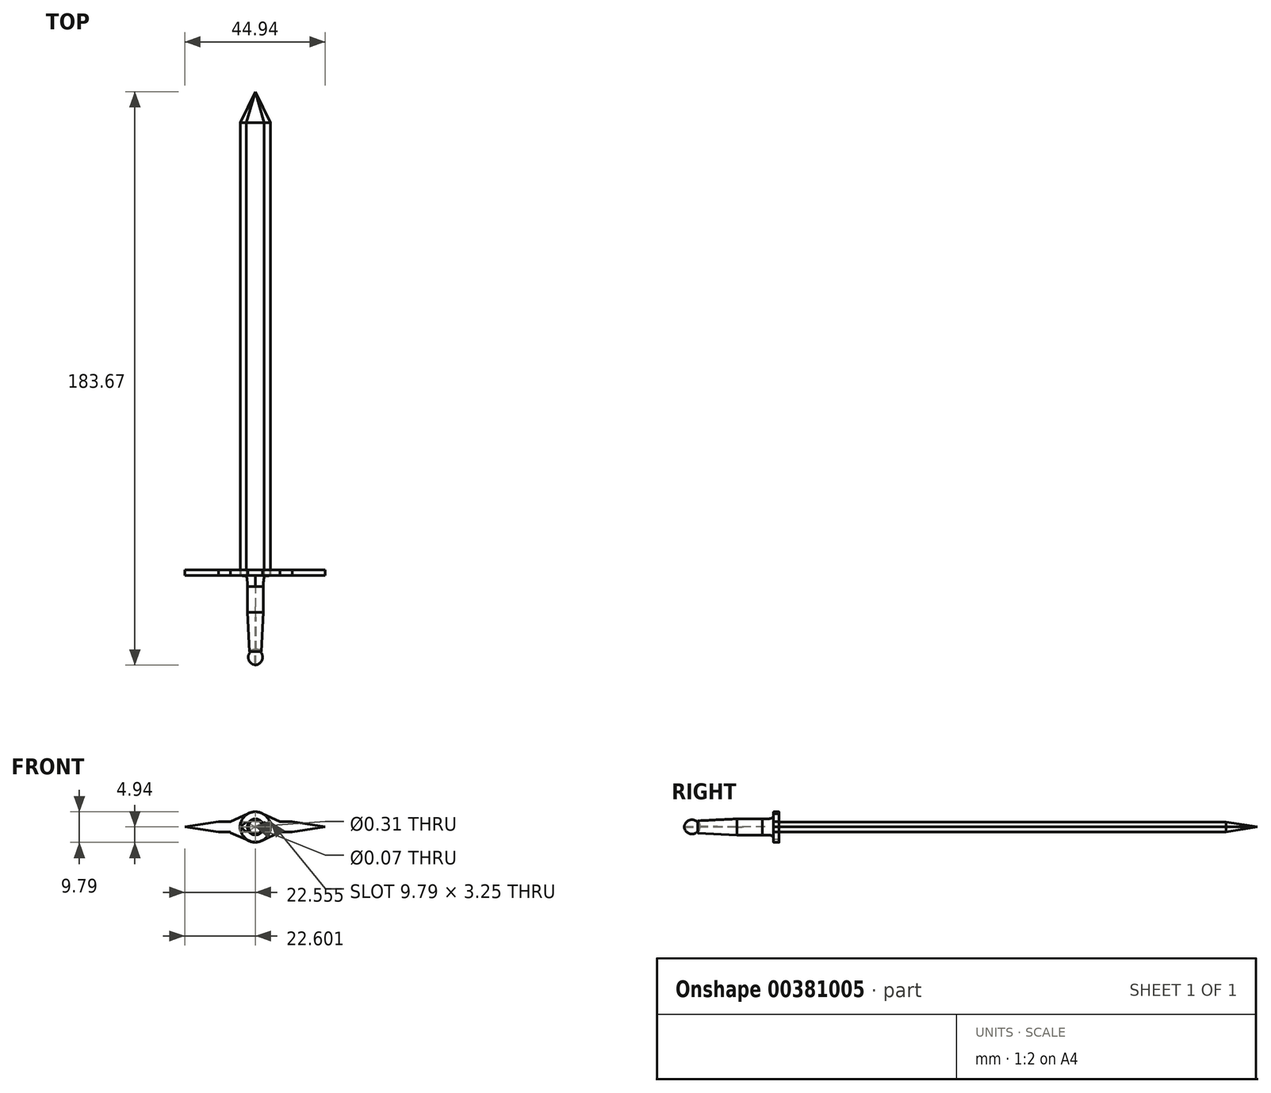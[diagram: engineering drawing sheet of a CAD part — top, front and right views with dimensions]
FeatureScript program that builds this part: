
annotation { "Feature Type Name" : "Feature", "Feature Type Description" : "" }
export const myFeature = defineFeature(function(context is Context, id is Id, definition is map)
    precondition{}
    {
        {
            var Q0;
            Q0=qCreatedBy(makeId("Top.planeOp"),FACE);
            var sketch = newSketch(context, id + "F0", { "sketchPlane" : qUnion([Q0])});
            skLineSegment(sketch, "E0", {"start": v(-127.1, -55.06) * mm, "end": v(-127.1, -61.54) * mm});
            skLineSegment(sketch, "E1", {"start": v(-127.7, -75.78) * mm, "end": v(-127.1, -63.23) * mm});
            skLineSegment(sketch, "E2", {"start": v(-124.83, -51.52) * mm, "end": v(-129.67, -51.52) * mm});
            skLineSegment(sketch, "E3", {"start": v(-129.67, -51.52) * mm, "end": v(-129.67, -54.16) * mm});
            skFitSpline(sketch, "E4", {"points": [v(-129.67, -54.16) * mm, v(-127.1, -55.06) * mm], "startDerivative": vector(4.15, -0.26) * mm, "endDerivative": vector(2.59, -2.32) * mm});
            skLineSegment(sketch, "E5", {"start": v(-127.1, -61.54) * mm, "end": v(-129.64, -61.54) * mm});
            skLineSegment(sketch, "E6", {"start": v(-129.64, -61.54) * mm, "end": v(-129.67, -54.16) * mm});
            skLineSegment(sketch, "E7", {"start": v(-129.64, -61.54) * mm, "end": v(-129.64, -63.25) * mm});
            skLineSegment(sketch, "E8", {"start": v(-129.64, -63.25) * mm, "end": v(-127.1, -63.23) * mm});
            skLineSegment(sketch, "E9", {"start": v(-129.64, -63.25) * mm, "end": v(-129.52, -75.1) * mm});
            skArc(sketch, "E10", {"start": v(-129.52, -75.1) * mm, "mid": v(-126.9, -77.63) * mm, "end": v(-129.52, -80.16) * mm});
            skLineSegment(sketch, "E11", {"start": v(-129.52, -75.1) * mm, "end": v(-129.52, -80.16) * mm});
            skLineSegment(sketch, "E12", {"start": v(-127.1, -61.54) * mm, "end": v(-127.1, -63.23) * mm});
            skFitSpline(sketch, "E13", {"points": [v(-127.1, -55.06) * mm, v(-124.83, -51.52) * mm], "startDerivative": vector(0.06, 10.63) * mm, "endDerivative": vector(6.8, 0) * mm});
            skSolve(sketch);
        }
        {
            var Q0;
            Q0=qSketchRegion(id+"F0",true);
            var Q1;
            Q1=sQuery(id+"F0.wireOp",EDGE,"E3");
            revolve(context, id + "F1", {"entities" : qUnion([Q0]), "axis" : qUnion([Q1]), "revolveType" : RevolveType.FULL});
        }
        {
            var Q0;
            {var subQ0=sQuery(id+"F0.wireOp",EDGE,"E2");Q0=makeQuery(id+"F1.opRevolve","SWEPT_FACE",FACE,{"disambiguationData":[OSD([subQ0]),TDD([makeQuery(id+"F0.imprint","IMPRINT",EDGE,{"disambiguationData":[TD([[makeQuery(id+"F0.imprint","INTERSECT",VERTEX,{"derivedFrom":[subQ0,sQuery(id+"F0.wireOp",EDGE,"E3")]}),1.0]])],"derivedFrom":subQ0})])]});}
            var sketch = newSketch(context, id + "F2", { "sketchPlane" : qUnion([Q0])});
            skLineSegment(sketch, "E14.bottom", {"start": v(141.43, 1.62) * mm, "end": v(117.91, 1.62) * mm});
            skLineSegment(sketch, "E14.top", {"start": v(141.43, -1.62) * mm, "end": v(117.91, -1.62) * mm});
            skLineSegment(sketch, "E14.left", {"start": v(141.43, 1.62) * mm, "end": v(141.43, -1.62) * mm});
            skLineSegment(sketch, "E14.right", {"start": v(117.91, 1.62) * mm, "end": v(117.91, -1.62) * mm});
            skPoint(sketch, "E14.middle", {"position": v(129.67, 0) * mm});
            skPoint(sketch, "E15.middle", {"position": v(129.67, 3.45) * mm});
            skPoint(sketch, "E16.middle", {"position": v(129.67, -1.62) * mm});
            skLineSegment(sketch, "E17", {"start": v(117.91, 1.62) * mm, "end": v(107.33, 0) * mm});
            skPoint(sketch, "E17.endSnap0", {"position": v(117.91, 0) * mm});
            skLineSegment(sketch, "E18", {"start": v(107.33, 0) * mm, "end": v(117.91, -1.62) * mm});
            skLineSegment(sketch, "E19", {"start": v(141.43, -1.62) * mm, "end": v(152.27, 0) * mm});
            skLineSegment(sketch, "E20", {"start": v(152.27, 0) * mm, "end": v(141.43, 1.62) * mm});
            skPoint(sketch, "E21", {"position": v(141.43, 0) * mm});
            skArc(sketch, "E22", {"start": v(125.1, 1.62) * mm, "mid": v(133.25, -3.43) * mm, "end": v(127.86, 4.49) * mm});
            skArc(sketch, "E23", {"start": v(127.86, 4.49) * mm, "mid": v(126.18, 3.35) * mm, "end": v(125.1, 1.62) * mm});
            skLineSegment(sketch, "E24", {"start": v(121.8, -1.62) * mm, "end": v(121.8, 1.62) * mm});
            skLineSegment(sketch, "E25", {"start": v(121.8, 1.62) * mm, "end": v(127.86, 4.49) * mm});
            skLineSegment(sketch, "E26", {"start": v(121.8, -1.62) * mm, "end": v(127.86, -4.59) * mm});
            skLineSegment(sketch, "E27", {"start": v(137.7, 1.62) * mm, "end": v(137.7, -1.91) * mm});
            skLineSegment(sketch, "E28", {"start": v(137.7, -1.91) * mm, "end": v(131.56, -4.46) * mm});
            skLineSegment(sketch, "E29", {"start": v(137.7, 1.62) * mm, "end": v(131.59, 4.47) * mm});
            skSolve(sketch);
        }
        {
            var Q0;
            Q0=qSketchRegion(id+"F2",true);
            extrude(context, id + "F3", {"entities" : qUnion([Q0]), "depth" : 1.78 * mm});
        }
        {
            var Q0;
            Q0=makeQuery(id+"F1.opRevolve","SWEPT_FACE",FACE,{"disambiguationData":[OSD([sQuery(id+"F0.wireOp",EDGE,"E2")])]});
            var sketch = newSketch(context, id + "F4", { "sketchPlane" : qUnion([Q0])});
            skLineSegment(sketch, "E30", {"start": v(124.83, 0) * mm, "end": v(126.83, 1.53) * mm});
            skLineSegment(sketch, "E31", {"start": v(124.83, 0) * mm, "end": v(126.83, -1.57) * mm});
            skLineSegment(sketch, "E32", {"start": v(134.5, 0) * mm, "end": v(132.53, 1.57) * mm});
            skLineSegment(sketch, "E33", {"start": v(134.5, 0) * mm, "end": v(132.56, -1.57) * mm});
            skLineSegment(sketch, "E34", {"start": v(132.56, -1.57) * mm, "end": v(126.83, -1.57) * mm});
            skLineSegment(sketch, "E35", {"start": v(126.83, 1.53) * mm, "end": v(132.53, 1.57) * mm});
            skSolve(sketch);
        }
        {
            var Q0;
            Q0=makeQuery(id+"F4.imprint","IMPRINT",FACE,{"disambiguationData":[TD([[makeQuery(id+"F4.imprint","IMPRINT",EDGE,{"derivedFrom":sQuery(id+"F4.wireOp",EDGE,"E30")}),-1.0]])]});
            extrude(context, id + "F5", {"entities" : qUnion([Q0]), "depth" : 145.03 * mm});
        }
        {
            var Q0;
            Q0=makeQuery(id+"F5.opExtrude","CAP_FACE",FACE,{"disambiguationData":[OSD([sQuery(id+"F4.wireOp",EDGE,"E30"),sQuery(id+"F4.wireOp",EDGE,"E31"),sQuery(id+"F4.wireOp",EDGE,"E32"),sQuery(id+"F4.wireOp",EDGE,"E33"),sQuery(id+"F4.wireOp",EDGE,"E34"),sQuery(id+"F4.wireOp",EDGE,"E35")])],"isStart":false});
            var sketch = newSketch(context, id + "F6", { "sketchPlane" : qUnion([Q0])});
            skLineSegment(sketch, "E36", {"start": v(124.83, 0) * mm, "end": v(129.4, 0) * mm});
            skLineSegment(sketch, "E37", {"start": v(129.4, 0) * mm, "end": v(134.5, 0) * mm});
            skLineSegment(sketch, "E38", {"start": v(129.4, 0) * mm, "end": v(126.83, 1.53) * mm});
            skLineSegment(sketch, "E39", {"start": v(129.4, 0) * mm, "end": v(132.53, 1.57) * mm});
            skLineSegment(sketch, "E40", {"start": v(129.4, 0) * mm, "end": v(126.83, -1.57) * mm});
            skLineSegment(sketch, "E41", {"start": v(129.4, 0) * mm, "end": v(132.56, -1.57) * mm});
            skLineSegment(sketch, "E42", {"start": v(126.83, 1.53) * mm, "end": v(124.83, 0) * mm});
            skLineSegment(sketch, "E43", {"start": v(126.83, -1.57) * mm, "end": v(124.83, 0) * mm});
            skLineSegment(sketch, "E44", {"start": v(132.53, 1.57) * mm, "end": v(134.5, 0) * mm});
            skLineSegment(sketch, "E45", {"start": v(132.56, -1.57) * mm, "end": v(134.5, 0) * mm});
            skLineSegment(sketch, "E46", {"start": v(132.53, 1.57) * mm, "end": v(126.83, 1.53) * mm});
            skLineSegment(sketch, "E47", {"start": v(126.83, -1.57) * mm, "end": v(132.56, -1.57) * mm});
            skSolve(sketch);
        }
        {
            var Q0;
            Q0=makeQuery(id+"F5.opExtrude","CAP_FACE",FACE,{"disambiguationData":[OSD([sQuery(id+"F4.wireOp",EDGE,"E30"),sQuery(id+"F4.wireOp",EDGE,"E31"),sQuery(id+"F4.wireOp",EDGE,"E32"),sQuery(id+"F4.wireOp",EDGE,"E33"),sQuery(id+"F4.wireOp",EDGE,"E34"),sQuery(id+"F4.wireOp",EDGE,"E35")])],"isStart":false});
            cPlane(context, id + "F7", {"entities" : qUnion([Q0]), "cplaneType" : CPlaneType.OFFSET, "offset" : 10 * mm, "width" : 150 * mm, "height" : 150 * mm});
        }
        {
            var Q0;
            Q0=qCreatedBy(id+"F7.planeOp",FACE);
            var sketch = newSketch(context, id + "F8", { "sketchPlane" : qUnion([Q0])});
            skPoint(sketch, "E48", {"position": v(129.72, 0) * mm});
            skSolve(sketch);
        }
        {
            var Q1;
            Q1=makeQuery(id+"F5.opExtrude","CAP_FACE",FACE,{"disambiguationData":[OSD([sQuery(id+"F4.wireOp",EDGE,"E30"),sQuery(id+"F4.wireOp",EDGE,"E31"),sQuery(id+"F4.wireOp",EDGE,"E32"),sQuery(id+"F4.wireOp",EDGE,"E33"),sQuery(id+"F4.wireOp",EDGE,"E34"),sQuery(id+"F4.wireOp",EDGE,"E35")])],"isStart":false});
            var Q2;
            Q2=sQuery(id+"F8.wireOp",VERTEX,"E48");
            loft(context, id + "F9", {"operationType" : NewBodyOperationType.ADD, "sheetProfilesArray" : [{ "sheetProfileEntities" : qUnion([Q1]) }, { "sheetProfileEntities" : qUnion([Q2]) }]});
        }
    });
